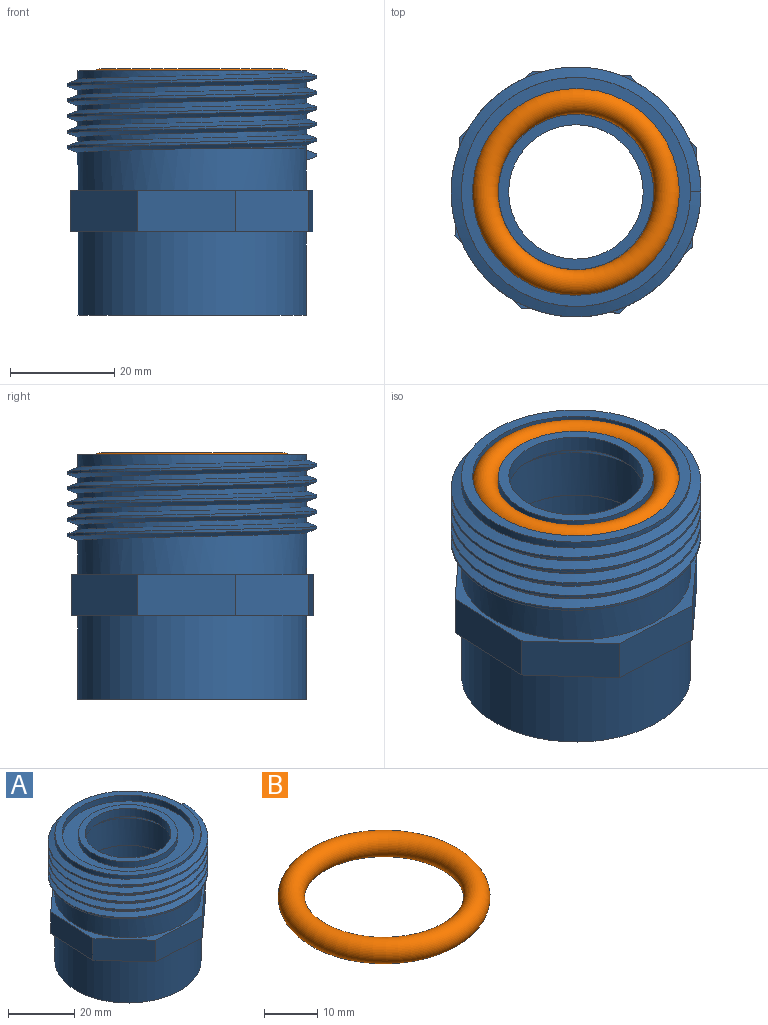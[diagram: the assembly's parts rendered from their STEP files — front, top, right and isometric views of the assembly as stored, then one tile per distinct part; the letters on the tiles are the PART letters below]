
ASSEMBLY  parts=2 mates=1
PART A: 38 faces, bbox 48x55.4x47 mm
  f0: plane 27.6x22.71mm, normal (0,0,-1), area 0.4mm2, adj f14,f24
  f1: cylinder r=19.85mm len=39.7mm, axis (0,0,-1), area 268.2mm2, adj f8,f10
  f2: cylinder r=22mm len=44mm, axis (0,0,-1), area 242mm2, adj f7,f8,f17,f20
  f3: cylinder r=22mm len=22mm, axis (0,0,-1), area 13mm2, adj f4,f9,f18,f27
  f4: cylinder r=22mm len=44mm, axis (0,0,-1), area 136.9mm2, adj f3,f5,f9,f18,f20
  f5: cylinder r=22mm len=44mm, axis (0,0,-1), area 138.2mm2, adj f4,f6,f18,f20
  f6: cylinder r=22mm len=44mm, axis (0,0,-1), area 138.2mm2, adj f5,f7,f18,f20
  f7: cylinder r=22mm len=44mm, axis (0,0,-1), area 138.2mm2, adj f2,f6,f18,f20
  f8: plane 44x44mm, normal (0,0,1), area 282.7mm2, adj f1,f2
  f9: plane 40.75x33.53mm, normal (0,0,-1), area 0.6mm2, adj f3,f4,f19,f25
  f10: plane 39.7x39.7mm, normal (0,0,1), area 540.4mm2, adj f1,f12
  f11: cylinder r=12.9mm len=25.8mm, axis (0,0,-1), area 243.2mm2, adj f13,f15
  f12: cylinder r=14.9mm len=29.8mm, axis (0,0,-1), area 201.3mm2, adj f10,f13
  f13: plane 29.8x29.8mm, normal (0,0,1), area 174.7mm2, adj f11,f12
  f14: cylinder r=14.9mm len=29.8mm, axis (0,0,-1), area 936.2mm2, adj f0,f15,f22
  f15: cone r=14.9mm half-angle=45deg, axis (0,0,-1), area 247mm2, adj f11,f14
  f16: plane 2x2mm, normal (0,-1,0), area 2.5mm2, adj f18,f19,f20,f21
  f17: plane 2x2mm, normal (0,1,0), area 2.5mm2, adj f2,f18,f20,f21
  f18: bspline ~55.43x48mm, area 1543.2mm2, adj f3,f4,f5,f6,f7,f16,f17,f19
  f19: cylinder r=22mm len=40.75mm, axis (0,0,1), area 91.6mm2, adj f9,f16,f18,f20,f25
  f20: bspline ~55.43x48mm, area 1542.5mm2, adj f2,f4,f5,f6,f7,f16,f17,f19
  f21: cylinder r=24mm len=48mm, axis (0,0,1), area 377mm2, adj f16,f17,f18,f20
  f22: plane 27.6x22.71mm, normal (0,0,1), area 0.4mm2, adj f14,f24
  f23: cylinder r=22mm len=44mm, axis (0,0,1), area 2211.7mm2, adj f26,f36
  f24: cylinder r=14.9mm len=32mm, axis (0,0,1), area 2995.8mm2, adj f0,f22,f26
  f25: cylinder r=22mm len=44mm, axis (0,0,1), area 1082.3mm2, adj f9,f18,f19,f27,f37
  f26: plane 44x44mm, normal (0,0,-1), area 823.1mm2, adj f23,f24
  f27: plane 18.93x10.48mm, normal (0,0,1), area 0.1mm2, adj f3,f18,f25
  f28: plane 18.87x8mm, normal (1,-0.05,0), area 151.1mm2, adj f29,f35,f36,f37
  f29: plane 13.99x12.7mm, normal (0.74,0.67,0), area 151.1mm2, adj f28,f30,f36,f37
  f30: plane 18.87x8mm, normal (0.05,1,0), area 151.1mm2, adj f29,f31,f36,f37
  f31: plane 13.99x12.7mm, normal (-0.67,0.74,0), area 151.1mm2, adj f30,f32,f36,f37
  f32: plane 18.87x8mm, normal (-1,0.05,0), area 151.1mm2, adj f31,f33,f36,f37
  f33: plane 13.99x12.7mm, normal (-0.74,-0.67,0), area 151.1mm2, adj f32,f34,f36,f37
  f34: plane 18.87x8mm, normal (-0.05,-1,0), area 151.1mm2, adj f33,f35,f36,f37
  f35: plane 13.99x12.7mm, normal (0.67,-0.74,0), area 151.1mm2, adj f28,f34,f36,f37
  f36: plane 46.47x46.47mm, normal (0,0,-1), area 203.1mm2, adj f23,f28,f29,f30,f31,f32,f33,f34
  f37: plane 46.47x46.47mm, normal (0,0,1), area 203.1mm2, adj f25,f28,f29,f30,f31,f32,f33,f34
PART B: 1 faces, bbox 43.3x43.3x5 mm
  f0: torus R=17.5mm, axis (0,0,1), area 1727.2mm2
PLACE A t=(-6.62,10.49,22.81)mm
PLACE B t=(-53.24,10.49,35.66)mm
MATE fastened B.f0 <-> A.f2  axis (0,0,1) through (-6.62,10.49,35.66)mm
